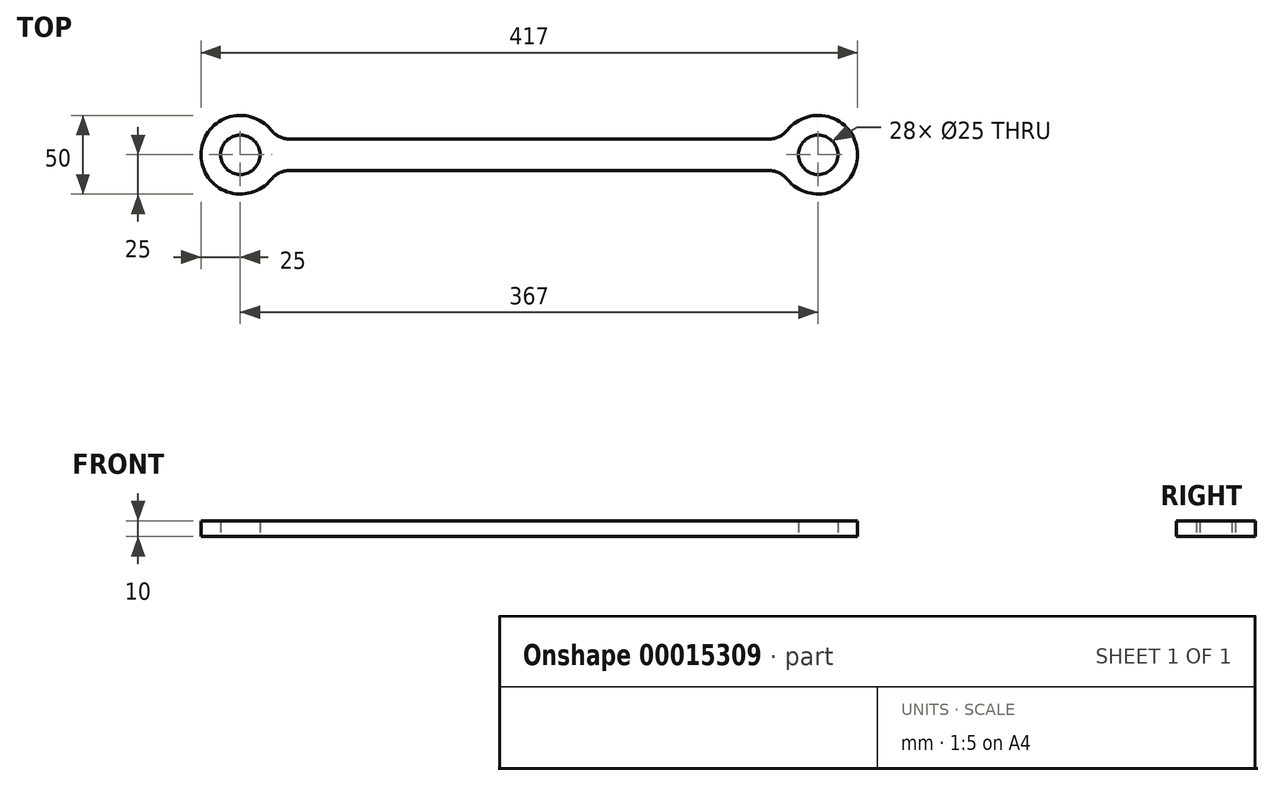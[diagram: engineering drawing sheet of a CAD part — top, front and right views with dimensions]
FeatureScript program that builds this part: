
annotation { "Feature Type Name" : "Feature", "Feature Type Description" : "" }
export const myFeature = defineFeature(function(context is Context, id is Id, definition is map)
    precondition{}
    {
        {
            var Q0;
            Q0=qCreatedBy(makeId("Top.planeOp"),FACE);
            var sketch = newSketch(context, id + "F0", { "sketchPlane" : qUnion([Q0])});
            skArc(sketch, "E0", {"start": v(19.52, 15.63) * mm, "mid": v(-25, 0) * mm, "end": v(19.52, -15.63) * mm});
            skArc(sketch, "E1", {"start": v(347.48, -15.62) * mm, "mid": v(392, 0) * mm, "end": v(347.48, 15.62) * mm});
            skLineSegment(sketch, "E2", {"start": v(31.22, 10) * mm, "end": v(335.78, 10) * mm});
            skLineSegment(sketch, "E3", {"start": v(0, 0) * mm, "end": v(367, 0) * mm, "construction": true});
            skLineSegment(sketch, "E4.MirrorCS", {"start": v(31.22, -10) * mm, "end": v(335.78, -10) * mm});
            skPoint(sketch, "E5.visualSharp", {"position": v(22.91, 10) * mm});
            skArc(sketch, "E5.filletArc", {"start": v(19.52, 15.62) * mm, "mid": v(24.73, 11.48) * mm, "end": v(31.22, 10) * mm});
            skPoint(sketch, "E6.visualSharp", {"position": v(22.91, -10) * mm});
            skArc(sketch, "E6.filletArc", {"start": v(31.22, -10) * mm, "mid": v(24.73, -11.48) * mm, "end": v(19.52, -15.62) * mm});
            skPoint(sketch, "E7.visualSharp", {"position": v(344.09, -10) * mm});
            skArc(sketch, "E7.filletArc", {"start": v(347.48, -15.62) * mm, "mid": v(342.27, -11.48) * mm, "end": v(335.78, -10) * mm});
            skPoint(sketch, "E8.visualSharp", {"position": v(344.09, 10) * mm});
            skArc(sketch, "E8.filletArc", {"start": v(335.78, 10) * mm, "mid": v(342.27, 11.48) * mm, "end": v(347.48, 15.63) * mm});
            skCircle(sketch, "E9", {"center": v(0, 0) * mm, "radius": 12.5 * mm});
            skCircle(sketch, "E10", {"center": v(367, 0) * mm, "radius": 12.5 * mm});
            skSolve(sketch);
        }
        {
            var Q0;
            Q0=qSketchRegion(id+"F0",true);
            extrude(context, id + "F1", {"entities" : qUnion([Q0]), "depth" : 10 * mm});
        }
    });
